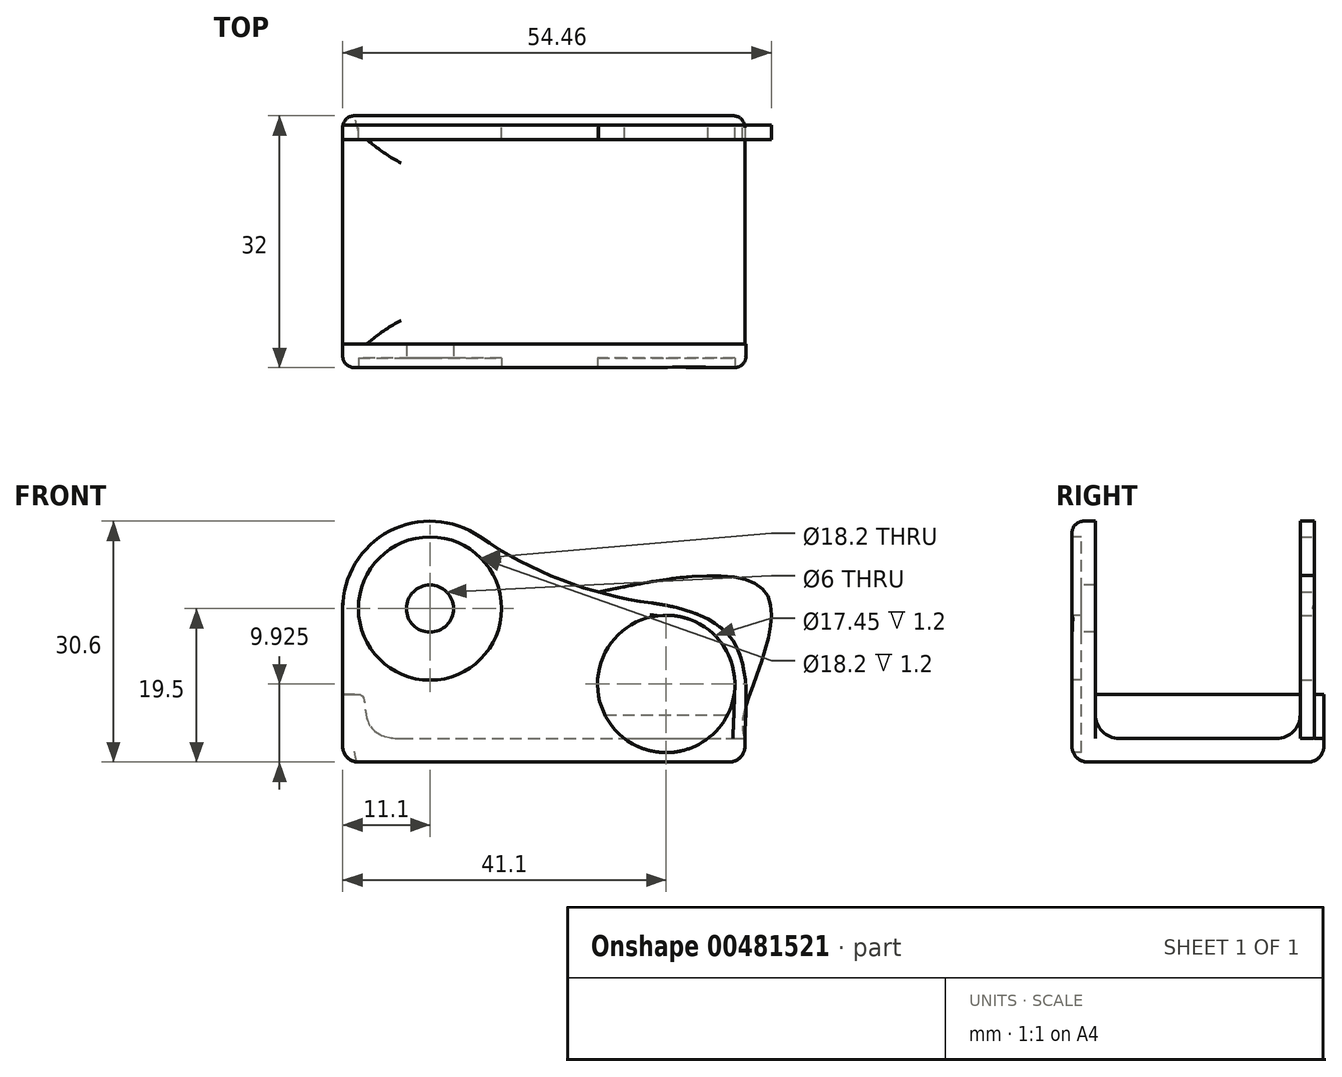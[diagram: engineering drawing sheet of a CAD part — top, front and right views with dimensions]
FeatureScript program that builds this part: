
annotation { "Feature Type Name" : "Feature", "Feature Type Description" : "" }
export const myFeature = defineFeature(function(context is Context, id is Id, definition is map)
    precondition{}
    {
        {
            var Q0;
            Q0=qCreatedBy(makeId("Front.planeOp"),FACE);
            var sketch = newSketch(context, id + "F0", { "sketchPlane" : qUnion([Q0])});
            skLineSegment(sketch, "E0.bottom", {"start": v(0, 0) * mm, "end": v(51.1, 0) * mm});
            skLineSegment(sketch, "E0.top", {"start": v(0, 3) * mm, "end": v(51.1, 3) * mm});
            skLineSegment(sketch, "E0.left", {"start": v(0, 0) * mm, "end": v(0, 3) * mm});
            skLineSegment(sketch, "E0.right", {"start": v(51.1, 0) * mm, "end": v(51.1, 3) * mm});
            skCircle(sketch, "E1", {"center": v(11.1, 19.5) * mm, "radius": 3 * mm});
            skCircle(sketch, "E2", {"center": v(11.1, 19.5) * mm, "radius": 9.1 * mm});
            skLineSegment(sketch, "E3", {"start": v(0, 3) * mm, "end": v(0, 19.5) * mm});
            skArc(sketch, "E4", {"start": v(17.4, 28.63) * mm, "mid": v(5.94, 29.33) * mm, "end": v(0, 19.5) * mm});
            skFitSpline(sketch, "E5", {"points": [v(22.2, 19.5) * mm, v(48.73, 16.46) * mm, v(51.1, 3) * mm], "startDerivative": vector(42.05, 8.29) * mm, "endDerivative": vector(0, -25.99) * mm});
            skArc(sketch, "E6.filletArc", {"start": v(17.4, 28.63) * mm, "mid": v(27.84, 23.12) * mm, "end": v(39.27, 20.2) * mm});
            skCircle(sketch, "E7", {"center": v(41.1, 9.92) * mm, "radius": 8.72 * mm});
            skLineSegment(sketch, "E8", {"start": v(0, 8.6) * mm, "end": v(2, 8.6) * mm});
            skLineSegment(sketch, "E9", {"start": v(2, 8.6) * mm, "end": v(2, 3) * mm});
            skFitSpline(sketch, "E10", {"points": [v(2, 8.6) * mm, v(7.45, 3) * mm], "startDerivative": vector(5.76, 0) * mm, "endDerivative": vector(19.43, 0) * mm});
            skSolve(sketch);
        }
        {
            var Q0;
            Q0=makeQuery(id+"F0.imprint","IMPRINT",FACE,{"disambiguationData":[TD([[makeQuery(id+"F0.imprint","IMPRINT",EDGE,{"derivedFrom":sQuery(id+"F0.wireOp",EDGE,"E2")}),-1.0]])]});
            var Q1;
            {var subQ4=sQuery(id+"F0.wireOp",EDGE,"E8");Q1=makeQuery(id+"F0.imprint","IMPRINT",FACE,{"disambiguationData":[TD([[makeQuery(id+"F0.imprint","IMPRINT",EDGE,{"derivedFrom":subQ4}),-1.0]])]});}
            var Q2;
            Q2=makeQuery(id+"F0.imprint","IMPRINT",FACE,{"disambiguationData":[TD([[makeQuery(id+"F0.imprint","IMPRINT",EDGE,{"derivedFrom":sQuery(id+"F0.wireOp",EDGE,"E0.bottom")}),1.0]])]});
            var Q3;
            {var subQ0=sQuery(id+"F0.wireOp",EDGE,"E7");var subQ1=sQuery(id+"F0.wireOp",EDGE,"E0.top");var subQ2=makeQuery(id+"F0.imprint","INTERSECT",VERTEX,{"disambiguationData":[OD(0.0)],"derivedFrom":[subQ1,subQ0]});Q3=makeQuery(id+"F0.imprint","IMPRINT",FACE,{"disambiguationData":[TD([[makeQuery(id+"F0.imprint","IMPRINT",EDGE,{"disambiguationData":[TD([[subQ2,-1.0]])],"derivedFrom":subQ1}),1.0]])]});}
            var Q4;
            {var subQ0=sQuery(id+"F0.wireOp",EDGE,"E7");var subQ1=sQuery(id+"F0.wireOp",EDGE,"E0.top");var subQ2=makeQuery(id+"F0.imprint","INTERSECT",VERTEX,{"disambiguationData":[OD(0.0)],"derivedFrom":[subQ1,subQ0]});Q4=makeQuery(id+"F0.imprint","IMPRINT",FACE,{"disambiguationData":[TD([[makeQuery(id+"F0.imprint","IMPRINT",EDGE,{"disambiguationData":[TD([[subQ2,-1.0]])],"derivedFrom":subQ1}),-1.0]])]});}
            var Q5;
            Q5=makeQuery(id+"F0.imprint","IMPRINT",FACE,{"disambiguationData":[TD([[makeQuery(id+"F0.imprint","IMPRINT",EDGE,{"derivedFrom":sQuery(id+"F0.wireOp",EDGE,"E1")}),-1.0]])]});
            var Q6;
            {var subQ0=sQuery(id+"F0.wireOp",EDGE,"E9");Q6=makeQuery(id+"F0.imprint","IMPRINT",FACE,{"disambiguationData":[TD([[makeQuery(id+"F0.imprint","IMPRINT",EDGE,{"derivedFrom":subQ0}),1.0]])]});}
            extrude(context, id + "F1", {"entities" : qUnion([Q0, Q1, Q2, Q3, Q4, Q5, Q6]), "oppositeDirection" : true, "depth" : 3 * mm, "offsetDistance" : 25 * mm});
        }
        {
            var Q0;
            {var subQ0=sQuery(id+"F0.wireOp",EDGE,"E7");var subQ1=sQuery(id+"F0.wireOp",EDGE,"E0.top");var subQ2=makeQuery(id+"F0.imprint","INTERSECT",VERTEX,{"disambiguationData":[OD(0.0)],"derivedFrom":[subQ1,subQ0]});Q0=makeQuery(id+"F0.imprint","IMPRINT",FACE,{"disambiguationData":[TD([[makeQuery(id+"F0.imprint","IMPRINT",EDGE,{"disambiguationData":[TD([[subQ2,-1.0]])],"derivedFrom":subQ1}),-1.0]])]});}
            var Q1;
            Q1=makeQuery(id+"F0.imprint","IMPRINT",FACE,{"disambiguationData":[TD([[makeQuery(id+"F0.imprint","IMPRINT",EDGE,{"derivedFrom":sQuery(id+"F0.wireOp",EDGE,"E0.bottom")}),1.0]])]});
            var Q2;
            {var subQ4=sQuery(id+"F0.wireOp",EDGE,"E8");Q2=makeQuery(id+"F0.imprint","IMPRINT",FACE,{"disambiguationData":[TD([[makeQuery(id+"F0.imprint","IMPRINT",EDGE,{"derivedFrom":subQ4}),-1.0]])]});}
            var Q3;
            {var subQ0=sQuery(id+"F0.wireOp",EDGE,"E9");Q3=makeQuery(id+"F0.imprint","IMPRINT",FACE,{"disambiguationData":[TD([[makeQuery(id+"F0.imprint","IMPRINT",EDGE,{"derivedFrom":subQ0}),1.0]])]});}
            extrude(context, id + "F2", {"entities" : qUnion([Q0, Q1, Q2, Q3]), "operationType" : NewBodyOperationType.ADD, "oppositeDirection" : true, "depth" : 32 * mm, "offsetDistance" : 25 * mm});
        }
        {
            var Q0;
            Q0=makeQuery(id+"F2.opExtrude","CAP_FACE",FACE,{"disambiguationData":[OSD([sQuery(id+"F0.wireOp",EDGE,"E0.bottom"),sQuery(id+"F0.wireOp",EDGE,"E0.top"),sQuery(id+"F0.wireOp",EDGE,"E0.left"),sQuery(id+"F0.wireOp",EDGE,"E0.right"),sQuery(id+"F0.wireOp",EDGE,"E3"),sQuery(id+"F0.wireOp",EDGE,"E8"),sQuery(id+"F0.wireOp",EDGE,"E9")])],"isStart":false});
            var sketch = newSketch(context, id + "F3", { "sketchPlane" : qUnion([Q0])});
            skLineSegment(sketch, "E11.0.0", {"start": v(-2, 3) * mm, "end": v(-35.8, 3) * mm});
            skArc(sketch, "E11.0.1", {"start": v(-35.8, 3) * mm, "mid": v(-41.1, 18.65) * mm, "end": v(-46.4, 3) * mm});
            skLineSegment(sketch, "E11.0.2", {"start": v(-46.4, 3) * mm, "end": v(-51.1, 3) * mm});
            skFitSpline(sketch, "E11.0.3", {"points": [v(-51.1, 3) * mm, v(-51.1, 6.61) * mm, v(-53.65, 21.68) * mm, v(-30.37, 21.11) * mm, v(-22.2, 19.5) * mm]});
            skArc(sketch, "E11.0.4", {"start": v(-39.27, 20.2) * mm, "mid": v(-27.84, 23.12) * mm, "end": v(-17.4, 28.63) * mm});
            skArc(sketch, "E11.0.5", {"start": v(-17.4, 28.63) * mm, "mid": v(-5.94, 29.33) * mm, "end": v(0, 19.5) * mm});
            skLineSegment(sketch, "E11.0.6", {"start": v(0, 19.5) * mm, "end": v(0, 8.6) * mm});
            skLineSegment(sketch, "E11.0.7", {"start": v(0, 8.6) * mm, "end": v(-2, 8.6) * mm});
            skLineSegment(sketch, "E11.0.8", {"start": v(-2, 8.6) * mm, "end": v(-2, 3) * mm});
            skCircle(sketch, "E11.1.0", {"center": v(-11.1, 19.5) * mm, "radius": 9.1 * mm});
            skArc(sketch, "E11.2.0", {"start": v(-46.4, 3) * mm, "mid": v(-41.1, 18.65) * mm, "end": v(-35.8, 3) * mm});
            skLineSegment(sketch, "E11.2.1", {"start": v(-35.8, 3) * mm, "end": v(-46.4, 3) * mm});
            skCircle(sketch, "E12.0", {"center": v(-11.1, 19.5) * mm, "radius": 3 * mm});
            skSolve(sketch);
        }
        {
            var Q0;
            Q0=makeQuery(id+"F3.imprint","IMPRINT",FACE,{"disambiguationData":[TD([[makeQuery(id+"F3.imprint","IMPRINT",EDGE,{"derivedFrom":sQuery(id+"F3.wireOp",EDGE,"E11.0.0")}),-1.0]])]});
            var Q1;
            Q1=makeQuery(id+"F3.imprint","IMPRINT",FACE,{"disambiguationData":[TD([[makeQuery(id+"F3.imprint","IMPRINT",EDGE,{"derivedFrom":sQuery(id+"F3.wireOp",EDGE,"E11.2.0")}),-1.0]])]});
            var Q2;
            Q2=makeQuery(id+"F3.imprint","IMPRINT",FACE,{"disambiguationData":[TD([[makeQuery(id+"F3.imprint","IMPRINT",EDGE,{"derivedFrom":sQuery(id+"F3.wireOp",EDGE,"E11.1.0")}),-1.0]])]});
            var Q3;
            Q3=makeQuery(id+"F3.imprint","IMPRINT",FACE,{"disambiguationData":[TD([[makeQuery(id+"F3.imprint","IMPRINT",EDGE,{"derivedFrom":sQuery(id+"F3.wireOp",EDGE,"E11.0.2")}),-1.0]])]});
            extrude(context, id + "F4", {"entities" : qUnion([Q0, Q1, Q2, Q3]), "operationType" : NewBodyOperationType.ADD, "oppositeDirection" : true, "depth" : 3 * mm, "offsetDistance" : 25 * mm});
        }
        {
            var Q0;
            Q0=makeQuery(id+"F0.imprint","IMPRINT",FACE,{"disambiguationData":[TD([[makeQuery(id+"F0.imprint","IMPRINT",EDGE,{"derivedFrom":sQuery(id+"F0.wireOp",EDGE,"E1")}),-1.0]])]});
            var Q1;
            {var subQ0=sQuery(id+"F0.wireOp",EDGE,"E7");var subQ1=sQuery(id+"F0.wireOp",EDGE,"E0.top");var subQ2=makeQuery(id+"F0.imprint","INTERSECT",VERTEX,{"disambiguationData":[OD(0.0)],"derivedFrom":[subQ1,subQ0]});Q1=makeQuery(id+"F0.imprint","IMPRINT",FACE,{"disambiguationData":[TD([[makeQuery(id+"F0.imprint","IMPRINT",EDGE,{"disambiguationData":[TD([[subQ2,-1.0]])],"derivedFrom":subQ1}),1.0]])]});}
            var Q2;
            {var subQ0=sQuery(id+"F0.wireOp",EDGE,"E7");var subQ1=sQuery(id+"F0.wireOp",EDGE,"E0.top");var subQ2=makeQuery(id+"F0.imprint","INTERSECT",VERTEX,{"disambiguationData":[OD(0.0)],"derivedFrom":[subQ1,subQ0]});Q2=makeQuery(id+"F0.imprint","IMPRINT",FACE,{"disambiguationData":[TD([[makeQuery(id+"F0.imprint","IMPRINT",EDGE,{"disambiguationData":[TD([[subQ2,-1.0]])],"derivedFrom":subQ1}),-1.0]])]});}
            extrude(context, id + "F5", {"entities" : qUnion([Q0, Q1, Q2]), "operationType" : NewBodyOperationType.REMOVE, "oppositeDirection" : true, "depth" : 1.2 * mm, "offsetDistance" : 25 * mm});
        }
        {
            var Q0;
            Q0=makeQuery(id+"F3.imprint","IMPRINT",FACE,{"disambiguationData":[TD([[makeQuery(id+"F3.imprint","IMPRINT",EDGE,{"derivedFrom":sQuery(id+"F3.wireOp",EDGE,"E11.1.0")}),-1.0]])]});
            extrude(context, id + "F6", {"entities" : qUnion([Q0]), "operationType" : NewBodyOperationType.REMOVE, "oppositeDirection" : true, "depth" : 1.2 * mm, "offsetDistance" : 25 * mm});
        }
        {
            var Q0;
            {var subQ0=sQuery(id+"F0.wireOp",EDGE,"E0.right");Q0=makeQuery(id+"F2.boolean.opBoolean","MERGE",FACE,{"derivedFrom":[makeQuery(id+"F1.opExtrude","SWEPT_FACE",FACE,{"disambiguationData":[OSD([subQ0])]}),makeQuery(id+"F2.opExtrude","SWEPT_FACE",FACE,{"disambiguationData":[OSD([subQ0])]})]});}
            var sketch = newSketch(context, id + "F7", { "sketchPlane" : qUnion([Q0])});
            skFitSpline(sketch, "E13.0", {"points": [v(3, 20.2) * mm, v(3, 14.47) * mm, v(3, 8.73) * mm, v(3, 3) * mm]});
            skFitSpline(sketch, "E13.1", {"points": [v(29, 3) * mm, v(29, 8.73) * mm, v(29, 14.47) * mm, v(29, 20.2) * mm]});
            skLineSegment(sketch, "E13.2", {"start": v(26, 3) * mm, "end": v(6, 3) * mm});
            skPoint(sketch, "E14.visualSharp", {"position": v(3, 3) * mm});
            skArc(sketch, "E14.filletArc", {"start": v(3, 6) * mm, "mid": v(3.88, 3.88) * mm, "end": v(6, 3) * mm});
            skPoint(sketch, "E15.visualSharp", {"position": v(29, 3) * mm});
            skArc(sketch, "E15.filletArc", {"start": v(26, 3) * mm, "mid": v(28.12, 3.88) * mm, "end": v(29, 6) * mm});
            skLineSegment(sketch, "E16", {"start": v(3, 6) * mm, "end": v(3, 3) * mm});
            skLineSegment(sketch, "E17", {"start": v(29, 6) * mm, "end": v(29, 3) * mm});
            skSolve(sketch);
        }
        {
            var Q0;
            {var subQ0=sQuery(id+"F7.wireOp",EDGE,"E14.filletArc");Q0=makeQuery(id+"F7.imprint","IMPRINT",FACE,{"disambiguationData":[TD([[makeQuery(id+"F7.imprint","IMPRINT",EDGE,{"derivedFrom":subQ0}),-1.0]])]});}
            var Q1;
            {var subQ0=sQuery(id+"F7.wireOp",EDGE,"E15.filletArc");Q1=makeQuery(id+"F7.imprint","IMPRINT",FACE,{"disambiguationData":[TD([[makeQuery(id+"F7.imprint","IMPRINT",EDGE,{"derivedFrom":subQ0}),-1.0]])]});}
            extrude(context, id + "F8", {"entities" : qUnion([Q0, Q1]), "operationType" : NewBodyOperationType.ADD, "oppositeDirection" : true, "depth" : 50 * mm, "offsetDistance" : 25 * mm});
        }
        {
            var Q0;
            Q0=makeQuery(id+"F4.boolean.opBoolean","MERGE",EDGE,{"derivedFrom":[makeQuery(id+"F2.opExtrude","CAP_EDGE",EDGE,{"disambiguationData":[OSD([sQuery(id+"F0.wireOp",EDGE,"E0.left"),sQuery(id+"F0.wireOp",EDGE,"E3")])],"isStart":false}),makeQuery(id+"F4.opExtrude","CAP_EDGE",EDGE,{"disambiguationData":[OSD([sQuery(id+"F3.wireOp",EDGE,"E11.0.6")])],"isStart":true})]});
            var Q1;
            Q1=makeQuery(id+"F1.opExtrude","CAP_EDGE",EDGE,{"disambiguationData":[OSD([sQuery(id+"F0.wireOp",EDGE,"E0.left"),sQuery(id+"F0.wireOp",EDGE,"E3")])],"isStart":true});
            var Q2;
            Q2=makeQuery(id+"F2.opExtrude","CAP_EDGE",EDGE,{"disambiguationData":[OSD([sQuery(id+"F0.wireOp",EDGE,"E0.right")])],"isStart":false});
            var Q3;
            Q3=makeQuery(id+"F4.opExtrude","CAP_EDGE",EDGE,{"disambiguationData":[OSD([sQuery(id+"F3.wireOp",EDGE,"E11.0.3")])],"isStart":true});
            var Q4;
            Q4=makeQuery(id+"F4.opExtrude","CAP_EDGE",EDGE,{"disambiguationData":[OSD([sQuery(id+"F3.wireOp",EDGE,"E11.0.4")])],"isStart":true});
            var Q5;
            Q5=makeQuery(id+"F4.opExtrude","CAP_EDGE",EDGE,{"disambiguationData":[OSD([sQuery(id+"F3.wireOp",EDGE,"E11.0.5")])],"isStart":true});
            var Q6;
            Q6=makeQuery(id+"F1.opExtrude","CAP_EDGE",EDGE,{"disambiguationData":[OSD([sQuery(id+"F0.wireOp",EDGE,"E0.right")])],"isStart":true});
            var Q7;
            Q7=makeQuery(id+"F1.opExtrude","CAP_EDGE",EDGE,{"disambiguationData":[OSD([sQuery(id+"F0.wireOp",EDGE,"E5")])],"isStart":true});
            var Q8;
            Q8=makeQuery(id+"F1.opExtrude","CAP_EDGE",EDGE,{"disambiguationData":[OSD([sQuery(id+"F0.wireOp",EDGE,"E6.filletArc")])],"isStart":true});
            var Q9;
            Q9=makeQuery(id+"F1.opExtrude","CAP_EDGE",EDGE,{"disambiguationData":[OSD([sQuery(id+"F0.wireOp",EDGE,"E4")])],"isStart":true});
            fillet(context, id + "F9", {"entities" : qUnion([Q0, Q1, Q2, Q3, Q4, Q5, Q6, Q7, Q8, Q9]), "radius" : 1.5 * mm, "allowEdgeOverflow" : false});
        }
        {
            var Q0;
            Q0=makeQuery(id+"F1.opExtrude","CAP_EDGE",EDGE,{"disambiguationData":[OSD([sQuery(id+"F0.wireOp",EDGE,"E0.bottom")])],"isStart":true});
            var Q1;
            {var subQ0=sQuery(id+"F0.wireOp",EDGE,"E0.right");var subQ1=sQuery(id+"F0.wireOp",EDGE,"E0.bottom");Q1=makeQuery(id+"F2.boolean.opBoolean","MERGE",EDGE,{"derivedFrom":[makeQuery(id+"F1.opExtrude","SWEPT_EDGE",EDGE,{"disambiguationData":[OSD([subQ1,subQ0])]}),makeQuery(id+"F2.opExtrude","SWEPT_EDGE",EDGE,{"disambiguationData":[OSD([subQ1,subQ0])]})]});}
            var Q2;
            {var subQ0=sQuery(id+"F0.wireOp",EDGE,"E0.bottom");Q2=makeQuery(id+"F9.opFillet","BLEND_EDGE",EDGE,{"blendedFrom":[makeQuery(id+"F1.opExtrude","CAP_EDGE",EDGE,{"disambiguationData":[OSD([sQuery(id+"F0.wireOp",EDGE,"E0.right")])],"isStart":true}),makeQuery(id+"F2.boolean.opBoolean","MERGE",FACE,{"derivedFrom":[makeQuery(id+"F1.opExtrude","SWEPT_FACE",FACE,{"disambiguationData":[OSD([subQ0])]}),makeQuery(id+"F2.opExtrude","SWEPT_FACE",FACE,{"disambiguationData":[OSD([subQ0])]})]})],"blendedInto":[makeQuery(id+"F2.boolean.opBoolean","MERGE",FACE,{"derivedFrom":[makeQuery(id+"F1.opExtrude","SWEPT_FACE",FACE,{"disambiguationData":[OSD([subQ0])]}),makeQuery(id+"F2.opExtrude","SWEPT_FACE",FACE,{"disambiguationData":[OSD([subQ0])]})]})]});}
            var Q3;
            Q3=makeQuery(id+"F2.opExtrude","CAP_EDGE",EDGE,{"disambiguationData":[OSD([sQuery(id+"F0.wireOp",EDGE,"E0.bottom")])],"isStart":false});
            var Q4;
            {var subQ0=sQuery(id+"F0.wireOp",EDGE,"E0.left");var subQ1=sQuery(id+"F0.wireOp",EDGE,"E0.bottom");Q4=makeQuery(id+"F2.boolean.opBoolean","MERGE",EDGE,{"derivedFrom":[makeQuery(id+"F1.opExtrude","SWEPT_EDGE",EDGE,{"disambiguationData":[OSD([subQ1,subQ0])]}),makeQuery(id+"F2.opExtrude","SWEPT_EDGE",EDGE,{"disambiguationData":[OSD([subQ1,subQ0])]})]});}
            var Q5;
            {var subQ0=sQuery(id+"F0.wireOp",EDGE,"E0.bottom");Q5=makeQuery(id+"F9.opFillet","BLEND_EDGE",EDGE,{"blendedFrom":[makeQuery(id+"F1.opExtrude","CAP_EDGE",EDGE,{"disambiguationData":[OSD([sQuery(id+"F0.wireOp",EDGE,"E0.left"),sQuery(id+"F0.wireOp",EDGE,"E3")])],"isStart":true}),makeQuery(id+"F2.boolean.opBoolean","MERGE",FACE,{"derivedFrom":[makeQuery(id+"F1.opExtrude","SWEPT_FACE",FACE,{"disambiguationData":[OSD([subQ0])]}),makeQuery(id+"F2.opExtrude","SWEPT_FACE",FACE,{"disambiguationData":[OSD([subQ0])]})]})],"blendedInto":[makeQuery(id+"F2.boolean.opBoolean","MERGE",FACE,{"derivedFrom":[makeQuery(id+"F1.opExtrude","SWEPT_FACE",FACE,{"disambiguationData":[OSD([subQ0])]}),makeQuery(id+"F2.opExtrude","SWEPT_FACE",FACE,{"disambiguationData":[OSD([subQ0])]})]})]});}
            var Q6;
            {var subQ0=sQuery(id+"F0.wireOp",EDGE,"E0.bottom");Q6=makeQuery(id+"F9.opFillet","BLEND_EDGE",EDGE,{"blendedFrom":[makeQuery(id+"F4.boolean.opBoolean","MERGE",EDGE,{"derivedFrom":[makeQuery(id+"F2.opExtrude","CAP_EDGE",EDGE,{"disambiguationData":[OSD([sQuery(id+"F0.wireOp",EDGE,"E0.left"),sQuery(id+"F0.wireOp",EDGE,"E3")])],"isStart":false}),makeQuery(id+"F4.opExtrude","CAP_EDGE",EDGE,{"disambiguationData":[OSD([sQuery(id+"F3.wireOp",EDGE,"E11.0.6")])],"isStart":true})]}),makeQuery(id+"F2.boolean.opBoolean","MERGE",FACE,{"derivedFrom":[makeQuery(id+"F1.opExtrude","SWEPT_FACE",FACE,{"disambiguationData":[OSD([subQ0])]}),makeQuery(id+"F2.opExtrude","SWEPT_FACE",FACE,{"disambiguationData":[OSD([subQ0])]})]})],"blendedInto":[makeQuery(id+"F2.boolean.opBoolean","MERGE",FACE,{"derivedFrom":[makeQuery(id+"F1.opExtrude","SWEPT_FACE",FACE,{"disambiguationData":[OSD([subQ0])]}),makeQuery(id+"F2.opExtrude","SWEPT_FACE",FACE,{"disambiguationData":[OSD([subQ0])]})]})]});}
            var Q7;
            {var subQ0=sQuery(id+"F0.wireOp",EDGE,"E0.bottom");Q7=makeQuery(id+"F9.opFillet","BLEND_EDGE",EDGE,{"blendedFrom":[makeQuery(id+"F2.opExtrude","CAP_EDGE",EDGE,{"disambiguationData":[OSD([sQuery(id+"F0.wireOp",EDGE,"E0.right")])],"isStart":false}),makeQuery(id+"F2.boolean.opBoolean","MERGE",FACE,{"derivedFrom":[makeQuery(id+"F1.opExtrude","SWEPT_FACE",FACE,{"disambiguationData":[OSD([subQ0])]}),makeQuery(id+"F2.opExtrude","SWEPT_FACE",FACE,{"disambiguationData":[OSD([subQ0])]})]})],"blendedInto":[makeQuery(id+"F2.boolean.opBoolean","MERGE",FACE,{"derivedFrom":[makeQuery(id+"F1.opExtrude","SWEPT_FACE",FACE,{"disambiguationData":[OSD([subQ0])]}),makeQuery(id+"F2.opExtrude","SWEPT_FACE",FACE,{"disambiguationData":[OSD([subQ0])]})]})]});}
            fillet(context, id + "F10", {"entities" : qUnion([Q0, Q1, Q2, Q3, Q4, Q5, Q6, Q7]), "radius" : 2 * mm, "allowEdgeOverflow" : false});
        }
    });
